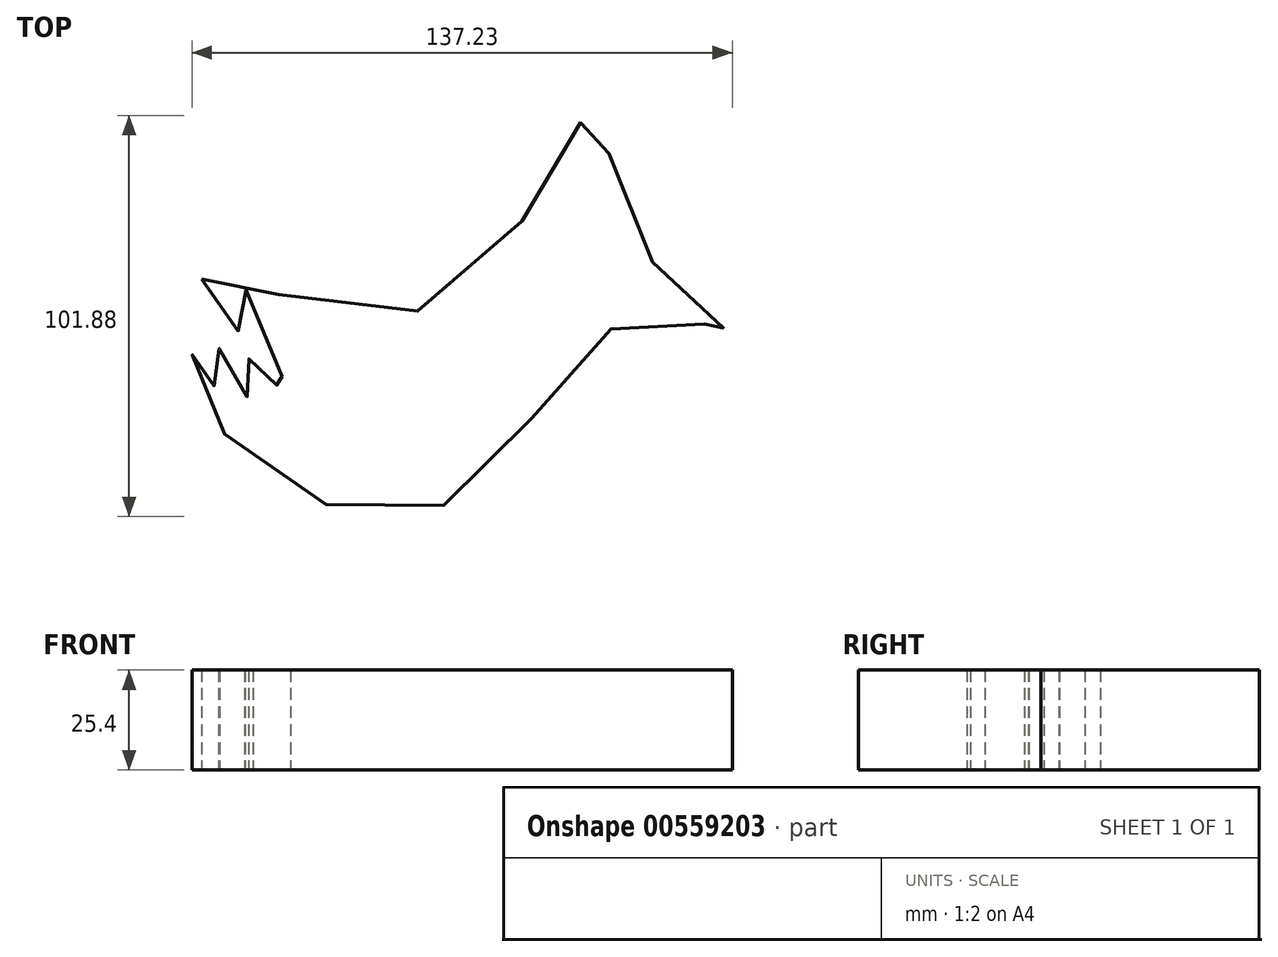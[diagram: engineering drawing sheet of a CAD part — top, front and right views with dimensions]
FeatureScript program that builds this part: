
annotation { "Feature Type Name" : "Feature", "Feature Type Description" : "" }
export const myFeature = defineFeature(function(context is Context, id is Id, definition is map)
    precondition{}
    {
        {
            var Q0;
            Q0=qCreatedBy(makeId("Top.planeOp"),FACE);
            var sketch = newSketch(context, id + "F0", { "sketchPlane" : qUnion([Q0])});
            skFitSpline(sketch, "E0", {"points": [v(-217.66, -137.68) * mm, v(-160.83, -145.3) * mm, v(-119.27, -96.17) * mm, v(-104.44, -131.31) * mm, v(-82.88, -151.63) * mm, v(-108.95, -148.11) * mm, v(-156.97, -195.5) * mm, v(-214.68, -173.1) * mm, v(-219.1, -156) * mm, v(-213.43, -165.83) * mm, v(-212.83, -154.6) * mm, v(-204.75, -169.53) * mm, v(-205.22, -154.76) * mm, v(-195.11, -170.41) * mm, v(-206.5, -140.45) * mm, v(-207.55, -150.73) * mm, v(-217.66, -137.68) * mm]});
            skSolve(sketch);
        }
        {
            var Q0;
            Q0 = qSketchRegion(id + "F0", true);
            extrude(context, id + "F1", {"entities" : qUnion([Q0]), "depth" : 25.4 * mm, "offsetDistance" : 25.4 * mm});
        }
    });
